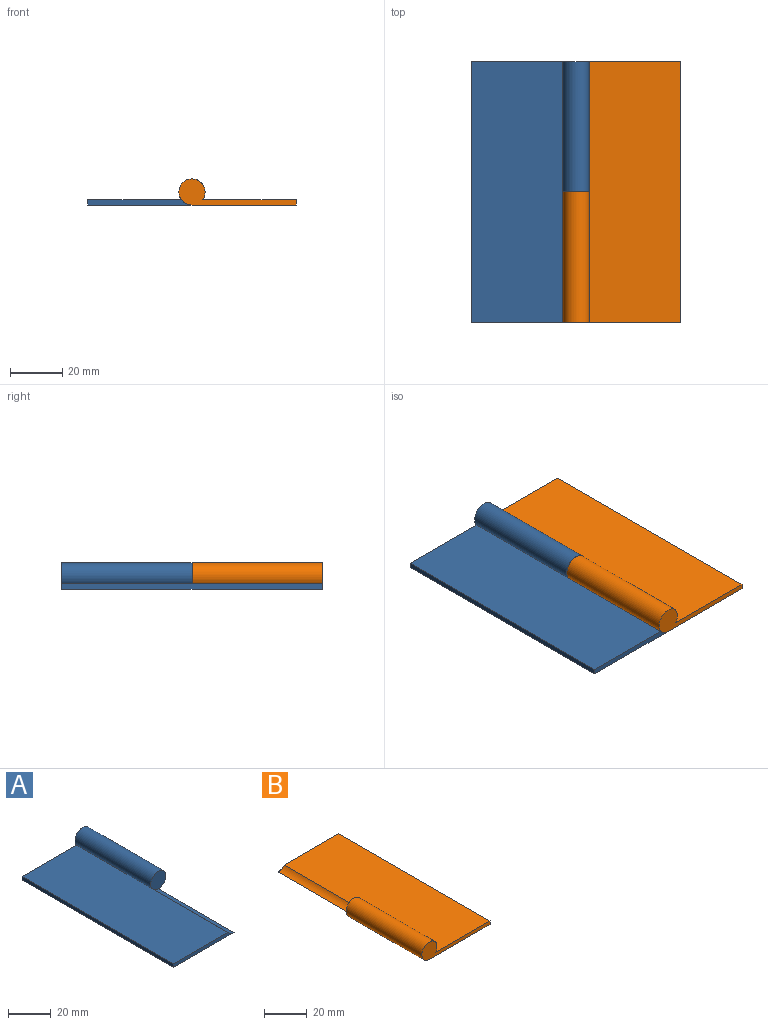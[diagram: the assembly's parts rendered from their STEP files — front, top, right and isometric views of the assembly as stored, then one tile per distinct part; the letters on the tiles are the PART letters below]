
ASSEMBLY  parts=2 mates=1
PART A: 8 faces, bbox 45x100x10 mm
  f0: plane 100x40mm, normal (0,0,-1), area 4000mm2, adj f1,f3,f4,f5,f6
  f1: cylinder r=5mm len=50mm, axis (0,1,0), area 231.8mm2, adj f0,f2,f4,f7
  f2: plane 100x36mm, normal (0,0,1), area 3600mm2, adj f1,f3,f4,f5,f6
  f3: plane 100x2mm, normal (-1,0,0), area 200mm2, adj f0,f2,f4,f5
  f4: plane 40x2mm, normal (0,-1,0), area 74.4mm2, adj f0,f1,f2,f3
  f5: plane 45x10mm, normal (0,1,0), area 152.9mm2, adj f0,f2,f3,f6
  f6: cylinder r=5mm len=50mm, axis (0,1,0), area 1339mm2, adj f0,f2,f5,f7
  f7: plane 10x10mm, normal (0,-1,0), area 78.5mm2, adj f1,f6
PART B: 8 faces, bbox 45x100x10 mm
  f0: cylinder r=5mm len=50mm, axis (0,1,0), area 231.8mm2, adj f1,f3,f5,f7
  f1: plane 100x40mm, normal (0,0,-1), area 4000mm2, adj f0,f2,f4,f5,f6
  f2: plane 100x2mm, normal (1,0,0), area 200mm2, adj f1,f3,f4,f5
  f3: plane 100x36mm, normal (0,0,1), area 3600mm2, adj f0,f2,f4,f5,f6
  f4: plane 45x10mm, normal (0,-1,0), area 152.9mm2, adj f1,f2,f3,f6
  f5: plane 40x2mm, normal (0,1,0), area 74.4mm2, adj f0,f1,f2,f3
  f6: cylinder r=5mm len=50mm, axis (0,1,0), area 1339mm2, adj f1,f3,f4,f7
  f7: plane 10x10mm, normal (0,1,0), area 78.5mm2, adj f0,f6
PLACE A t=(-52.83,-6.63,18.07)mm
PLACE B t=(-52.83,-6.63,18.07)mm
MATE revolute A.f6 <-> B.f0  axis (0,1,0) through (-52.83,-56.63,18.07)mm
